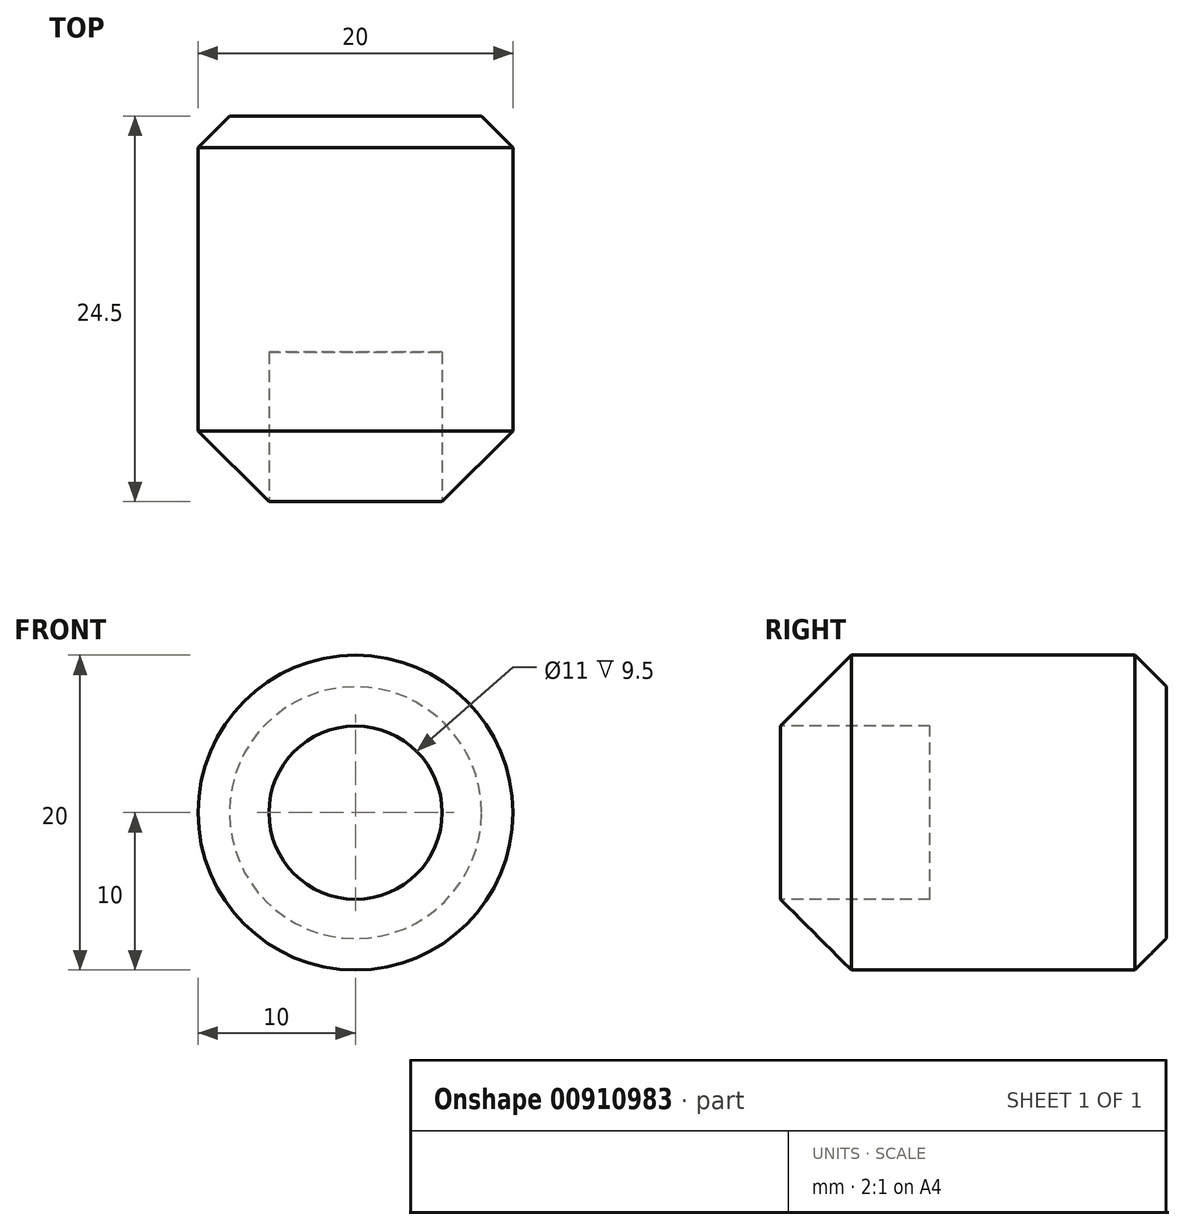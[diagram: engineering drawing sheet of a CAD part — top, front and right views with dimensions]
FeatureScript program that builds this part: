
annotation { "Feature Type Name" : "Feature", "Feature Type Description" : "" }
export const myFeature = defineFeature(function(context is Context, id is Id, definition is map)
    precondition{}
    {
        {
            var Q0;
            Q0=qCreatedBy(makeId("Front.planeOp"),FACE);
            var sketch = newSketch(context, id + "F0", { "sketchPlane" : qUnion([Q0])});
            skCircle(sketch, "E0", {"center": v(0, 0) * mm, "radius": 10 * mm});
            skSolve(sketch);
        }
        {
            var Q0;
            Q0=makeQuery(id+"F0.imprint","IMPRINT",FACE,{"disambiguationData":[TD([[makeQuery(id+"F0.imprint","IMPRINT",EDGE,{"derivedFrom":sQuery(id+"F0.wireOp",EDGE,"E0")}),1.0]])]});
            extrude(context, id + "F1", {"entities" : qUnion([Q0]), "depth" : 25 * mm, "offsetDistance" : 25 * mm});
        }
        {
            var Q0;
            Q0=makeQuery(id+"F1.opExtrude","CAP_FACE",FACE,{"disambiguationData":[OSD([sQuery(id+"F0.wireOp",EDGE,"E0")])],"isStart":false});
            var sketch = newSketch(context, id + "F2", { "sketchPlane" : qUnion([Q0])});
            skCircle(sketch, "E1", {"center": v(0, 0) * mm, "radius": 5.5 * mm});
            skSolve(sketch);
        }
        {
            var Q0;
            Q0=makeQuery(id+"F2.imprint","IMPRINT",FACE,{"disambiguationData":[TD([[makeQuery(id+"F2.imprint","IMPRINT",EDGE,{"derivedFrom":sQuery(id+"F2.wireOp",EDGE,"E1")}),1.0]])]});
            extrude(context, id + "F3", {"entities" : qUnion([Q0]), "operationType" : NewBodyOperationType.REMOVE, "oppositeDirection" : true, "depth" : 10 * mm, "offsetDistance" : 25 * mm});
        }
        {
            var Q0;
            Q0=makeQuery(id+"F1.opExtrude","CAP_EDGE",EDGE,{"disambiguationData":[OSD([sQuery(id+"F0.wireOp",EDGE,"E0")])],"isStart":true});
            chamfer(context, id + "F4", {"entities" : qUnion([Q0]), "width" : 2 * mm, "tangentPropagation" : true});
        }
        {
            var Q0;
            Q0=makeQuery(id+"F1.opExtrude","CAP_EDGE",EDGE,{"disambiguationData":[OSD([sQuery(id+"F0.wireOp",EDGE,"E0")])],"isStart":false});
            chamfer(context, id + "F5", {"entities" : qUnion([Q0]), "width" : 5 * mm, "tangentPropagation" : true});
        }
    });
